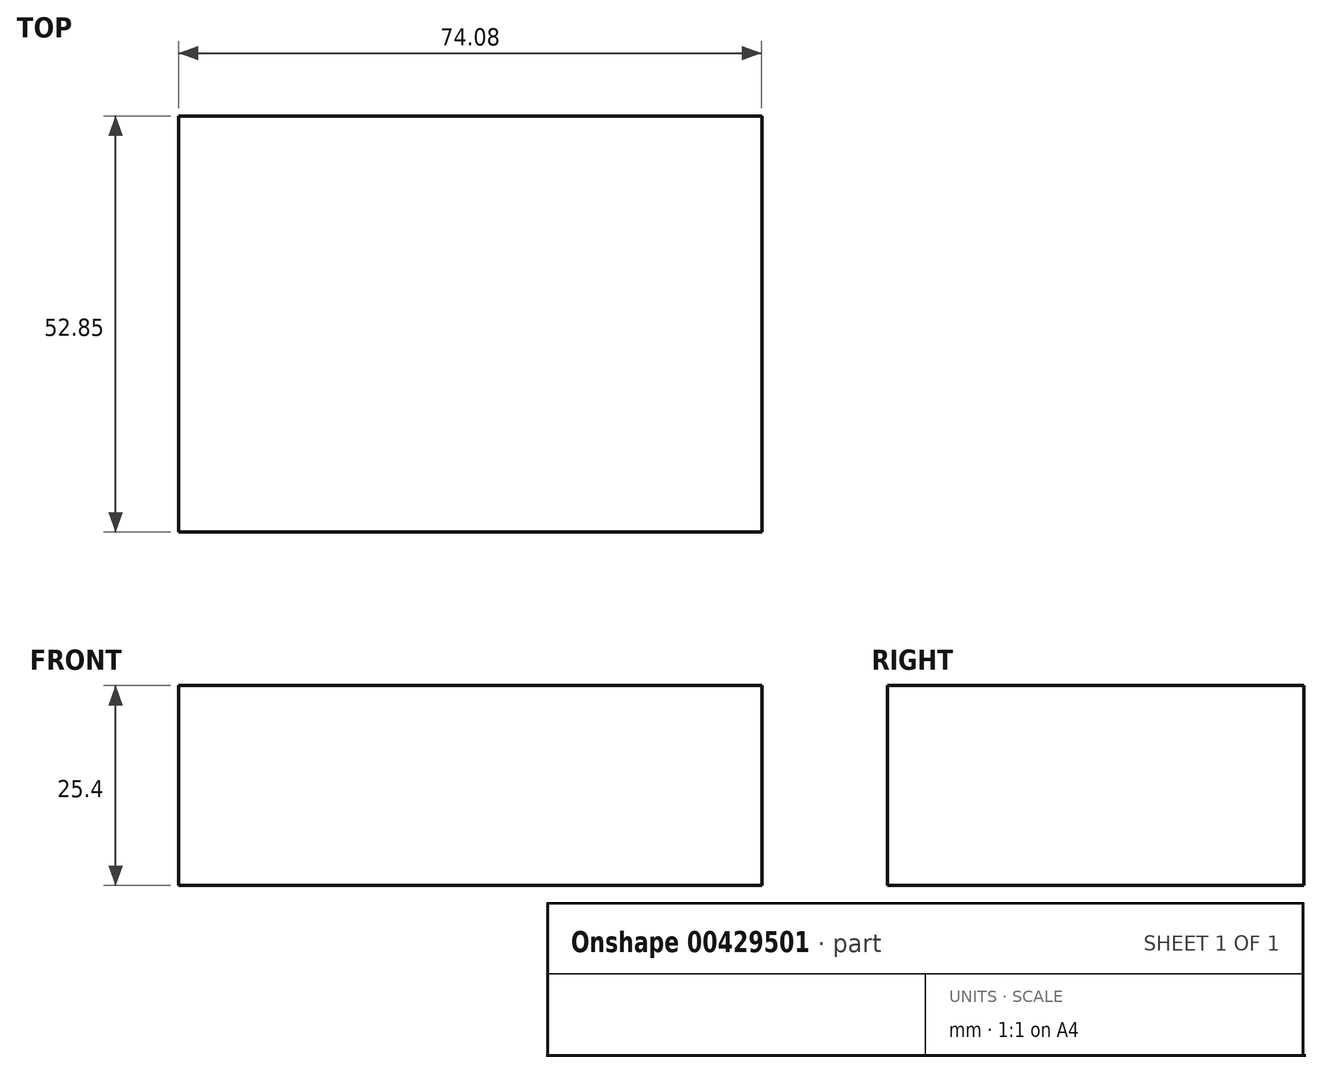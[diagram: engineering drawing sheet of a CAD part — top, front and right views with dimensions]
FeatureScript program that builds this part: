
annotation { "Feature Type Name" : "Feature", "Feature Type Description" : "" }
export const myFeature = defineFeature(function(context is Context, id is Id, definition is map)
    precondition{}
    {
        {
            var Q0;
            Q0=qCreatedBy(makeId("Top.planeOp"),FACE);
            var sketch = newSketch(context, id + "F0", { "sketchPlane" : qUnion([Q0])});
            skLineSegment(sketch, "E0.bottom", {"start": v(0, 0) * mm, "end": v(74.08, 0) * mm});
            skLineSegment(sketch, "E0.top", {"start": v(0, -52.85) * mm, "end": v(74.08, -52.85) * mm});
            skLineSegment(sketch, "E0.left", {"start": v(0, 0) * mm, "end": v(0, -52.85) * mm});
            skLineSegment(sketch, "E0.right", {"start": v(74.08, 0) * mm, "end": v(74.08, -52.85) * mm});
            skSolve(sketch);
        }
        {
            var Q0;
            Q0=makeQuery(id+"F0.imprint","IMPRINT",FACE,{"disambiguationData":[TD([[makeQuery(id+"F0.imprint","IMPRINT",EDGE,{"derivedFrom":sQuery(id+"F0.wireOp",EDGE,"E0.bottom")}),-1.0]])]});
            extrude(context, id + "F1", {"entities" : qUnion([Q0]), "depth" : 25.4 * mm});
        }
    });
